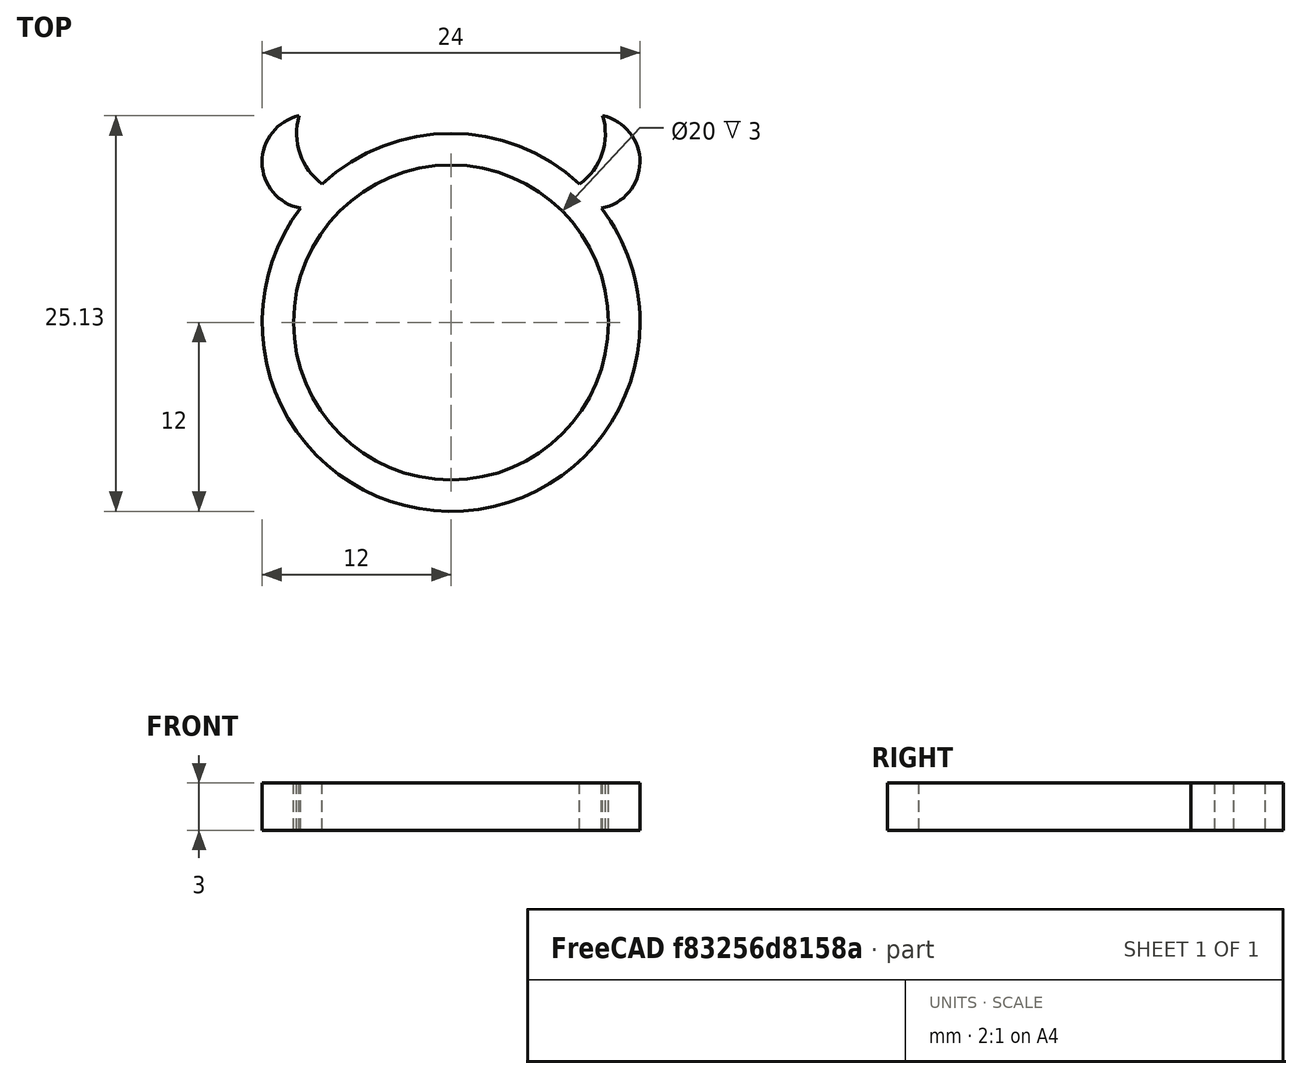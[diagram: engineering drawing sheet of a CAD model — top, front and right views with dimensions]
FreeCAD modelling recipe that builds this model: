
FCSTD DOCUMENT  (FreeCAD 0.17R13217 (Git))
Label: anillo-diablillo
License: All rights reserved
LicenseURL: http://en.wikipedia.org/wiki/All_rights_reserved
objects: Part::Cylinder×4, Part::Cut×2, Part::MultiFuse×2, Part::Mirroring×1
note: 9 computed .brp shape members not serialized (recipe doc carries the construction recipe); baked Part::Feature solids carry a one-line shape summary decoded from their .brp

FEATURE [Part::Cylinder] Cylinder  label="Cilindro"
  Angle = 360
  AttacherType = Attacher::AttachEngine3D
  Height = 3
  Radius = 12
FEATURE [Part::Cylinder] Cylinder001  label="Cilindro001"
  Angle = 360
  AttacherType = Attacher::AttachEngine3D
  Height = 10
  Placement = pos=(0,0,-4) rot=(0,0,1;0rad)
  Radius = 10
FEATURE [Part::Cut] Cut
  Base = -> Cylinder
  Refine = true
  Tool = -> Cylinder001
FEATURE [Part::Cylinder] Cylinder002  label="Cilindro002"
  Angle = 360
  AttacherType = Attacher::AttachEngine3D
  Height = 3
  Radius = 3
FEATURE [Part::Cylinder] Cylinder003  label="Cilindro003"
  Angle = 360
  AttacherType = Attacher::AttachEngine3D
  Height = 10
  Placement = pos=(3.2,1.8,0) rot=(0,0,1;0rad)
  Radius = 4
FEATURE [Part::Cut] Cut001
  Base = -> Cylinder002
  Placement = pos=(-9,10.2,0) rot=(0,0,1;0rad)
  Refine = true
  Tool = -> Cylinder003
FEATURE [Part::Mirroring] Part__Mirroring  label="Cut001 (Mirror #1)"
  Base = (0,0,0)
  Normal = (1,0,0)
  Source = -> Cut001
FEATURE [Part::MultiFuse] Fusion
  Refine = true
  Shapes = -> [Part__Mirroring,Cut001]
FEATURE [Part::MultiFuse] Fusion001
  Refine = true
  Shapes = -> [Cut,Fusion]
